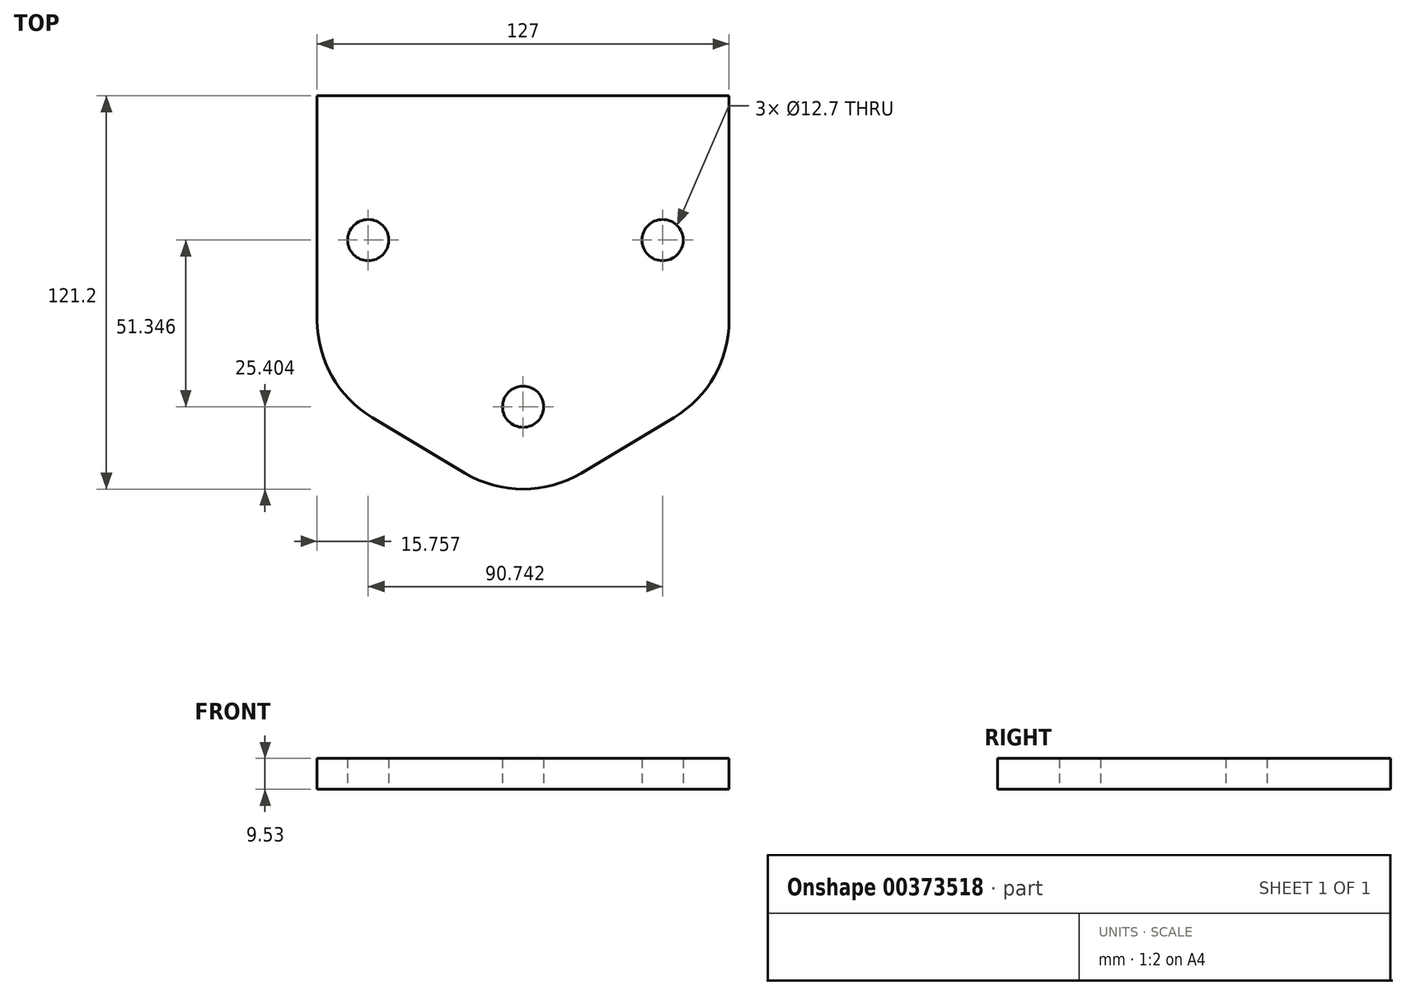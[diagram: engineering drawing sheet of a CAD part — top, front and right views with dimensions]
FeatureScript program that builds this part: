
annotation { "Feature Type Name" : "Feature", "Feature Type Description" : "" }
export const myFeature = defineFeature(function(context is Context, id is Id, definition is map)
    precondition{}
    {
        {
            var Q0;
            Q0=qCreatedBy(makeId("Top.planeOp"), FACE);
            var sketch = newSketch(context, id + "F0", { "sketchPlane" : qUnion([Q0])});
            skLineSegment(sketch, "E0.bottom", {"start": v(-63.5, 63.5) * mm, "end": v(63.5, 63.5) * mm});
            skLineSegment(sketch, "E0.top", {"start": v(-63.5, -63.5) * mm, "end": v(63.5, -63.5) * mm});
            skLineSegment(sketch, "E0.left", {"start": v(-63.5, 63.5) * mm, "end": v(-63.5, -5.63) * mm});
            skLineSegment(sketch, "E0.right", {"start": v(63.5, 63.5) * mm, "end": v(63.5, -5.63) * mm});
            skCircle(sketch, "E1", {"center": v(0, -32.3) * mm, "radius": 6.35 * mm});
            skCircle(sketch, "E2", {"center": v(-47.74, 19.05) * mm, "radius": 6.35 * mm});
            skCircle(sketch, "E3", {"center": v(43, 19.05) * mm, "radius": 6.35 * mm});
            skLineSegment(sketch, "E4", {"start": v(-17.97, -52.72) * mm, "end": v(-46.54, -35.57) * mm});
            skLineSegment(sketch, "E5.MirrorCS", {"start": v(17.97, -52.72) * mm, "end": v(46.54, -35.57) * mm});
            skPoint(sketch, "E6.visualSharp", {"position": v(0, -63.5) * mm});
            skArc(sketch, "E6.filletArc", {"start": v(-17.97, -52.72) * mm, "mid": v(0, -57.7) * mm, "end": v(17.97, -52.72) * mm});
            skPoint(sketch, "E7.newPointA", {"position": v(-63.5, -25.4) * mm});
            skArc(sketch, "E7.filletArc", {"start": v(-63.5, -5.63) * mm, "mid": v(-58.97, -22.83) * mm, "end": v(-46.54, -35.57) * mm});
            skPoint(sketch, "E8.newPointA", {"position": v(63.5, -25.4) * mm});
            skArc(sketch, "E8.filletArc", {"start": v(46.54, -35.57) * mm, "mid": v(58.97, -22.83) * mm, "end": v(63.5, -5.63) * mm});
            skSolve(sketch);
        }
        {
            var Q0;
            Q0 = qSketchRegion(id + "F0", true);
            extrude(context, id + "F1", {"entities" : qUnion([Q0]), "depth" : 9.52 * mm, "offsetDistance" : 25.4 * mm});
        }
    });
